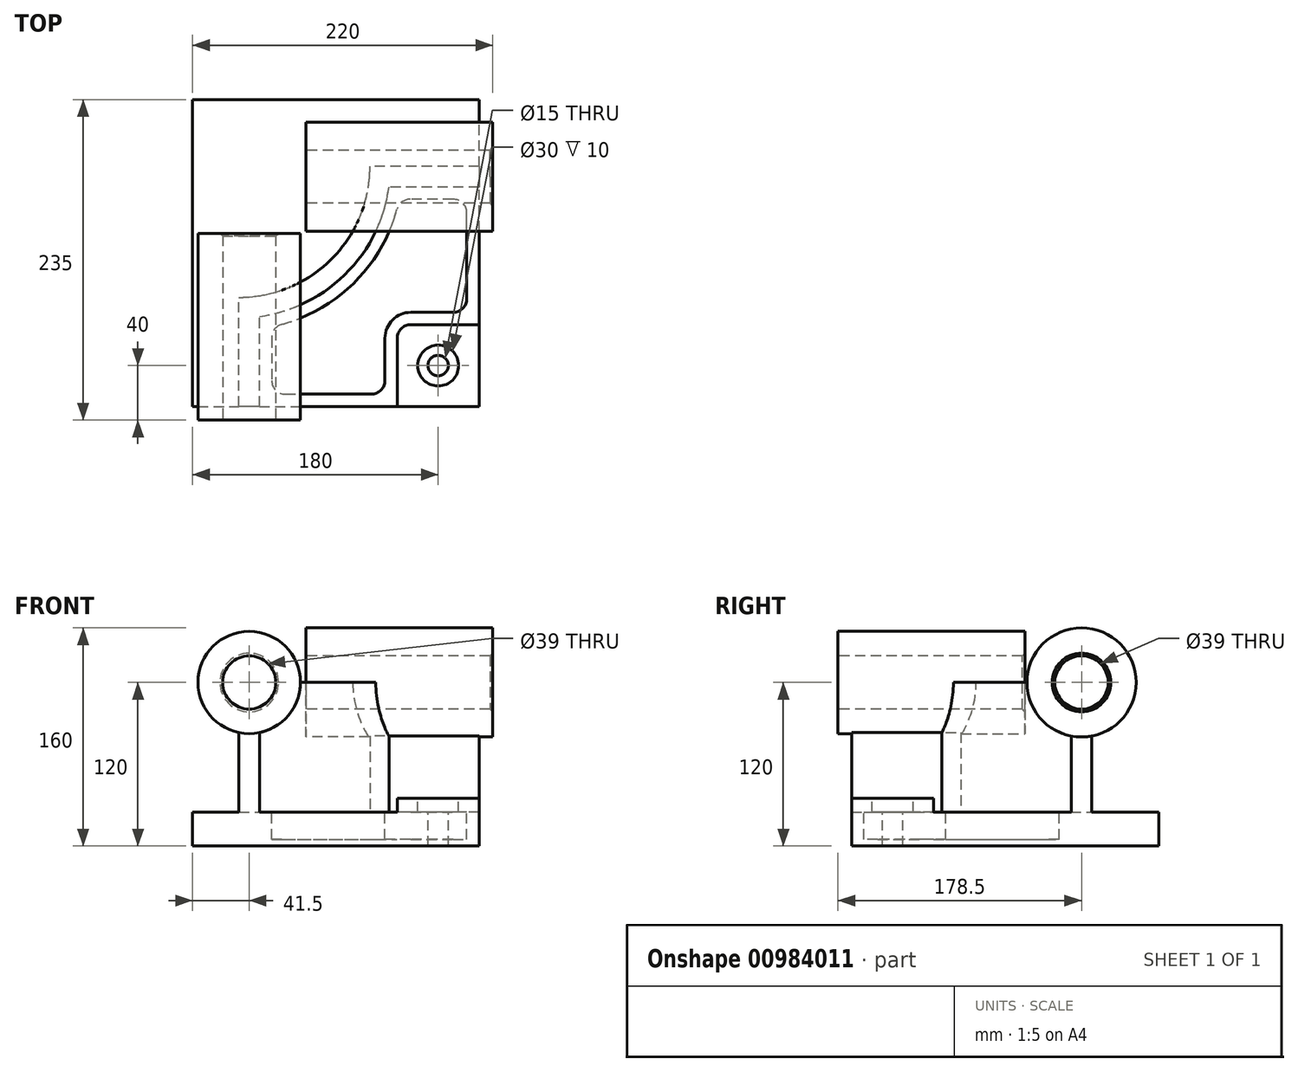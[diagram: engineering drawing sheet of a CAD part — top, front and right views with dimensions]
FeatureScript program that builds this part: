
annotation { "Feature Type Name" : "Feature", "Feature Type Description" : "" }
export const myFeature = defineFeature(function(context is Context, id is Id, definition is map)
    precondition{}
    {
        {
            var Q0;
            Q0=qCreatedBy(makeId("Top.planeOp"),FACE);
            var sketch = newSketch(context, id + "F0", { "sketchPlane" : qUnion([Q0])});
            skLineSegment(sketch, "E0.bottom", {"start": v(-105, -112.5) * mm, "end": v(105, -112.5) * mm});
            skLineSegment(sketch, "E0.top", {"start": v(-105, 112.5) * mm, "end": v(105, 112.5) * mm});
            skLineSegment(sketch, "E0.left", {"start": v(-105, -112.5) * mm, "end": v(-105, 112.5) * mm});
            skLineSegment(sketch, "E0.right", {"start": v(105, -112.5) * mm, "end": v(105, 112.5) * mm});
            skPoint(sketch, "E0.middle", {"position": v(0, 0) * mm});
            skSolve(sketch);
        }
        {
            var Q0;
            Q0=makeQuery(id+"F0.imprint","IMPRINT",FACE,{"disambiguationData":[TD([[makeQuery(id+"F0.imprint","IMPRINT",EDGE,{"derivedFrom":sQuery(id+"F0.wireOp",EDGE,"E0.bottom")}),1.0]])]});
            extrude(context, id + "F1", {"entities" : qUnion([Q0]), "depth" : 25 * mm, "offsetDistance" : 25 * mm});
        }
        {
            var Q0;
            Q0=makeQuery(id+"F1.opExtrude","CAP_FACE",FACE,{"disambiguationData":[OSD([sQuery(id+"F0.wireOp",EDGE,"E0.bottom"),sQuery(id+"F0.wireOp",EDGE,"E0.top"),sQuery(id+"F0.wireOp",EDGE,"E0.left"),sQuery(id+"F0.wireOp",EDGE,"E0.right")])],"isStart":false});
            var sketch = newSketch(context, id + "F2", { "sketchPlane" : qUnion([Q0])});
            skLineSegment(sketch, "E1", {"start": v(-71, -112.5) * mm, "end": v(-71, -32.5) * mm});
            skLineSegment(sketch, "E2", {"start": v(105, 63.5) * mm, "end": v(25, 63.5) * mm});
            skArc(sketch, "E3", {"start": v(-71, -32.5) * mm, "mid": v(-3.12, -4.38) * mm, "end": v(25, 63.5) * mm});
            skLineSegment(sketch, "E4", {"start": v(-71, 63.5) * mm, "end": v(25, 63.5) * mm, "construction": true});
            skLineSegment(sketch, "E5", {"start": v(-71, 63.5) * mm, "end": v(-71, -32.5) * mm, "construction": true});
            skLineSegment(sketch, "E6.0", {"start": v(-56, -112.5) * mm, "end": v(-56, -46.48) * mm});
            skArc(sketch, "E6.1", {"start": v(-56, -46.48) * mm, "mid": v(7.49, -14.99) * mm, "end": v(38.98, 48.5) * mm});
            skLineSegment(sketch, "E6.2", {"start": v(105, 48.5) * mm, "end": v(38.98, 48.5) * mm});
            skSolve(sketch);
        }
        {
            var Q0;
            {var subQ4=sQuery(id+"F2.wireOp",EDGE,"E1");Q0=makeQuery(id+"F2.imprint","IMPRINT",FACE,{"disambiguationData":[TD([[makeQuery(id+"F2.imprint","IMPRINT",EDGE,{"derivedFrom":subQ4}),-1.0]])]});}
            extrude(context, id + "F3", {"entities" : qUnion([Q0]), "operationType" : NewBodyOperationType.ADD, "depth" : 95 * mm, "offsetDistance" : 25 * mm});
        }
        {
            var Q0;
            {var subQ0=sQuery(id+"F0.wireOp",EDGE,"E0.bottom");Q0=makeQuery(id+"F3.boolean.opBoolean","MERGE",FACE,{"derivedFrom":[makeQuery(id+"F1.opExtrude","SWEPT_FACE",FACE,{"disambiguationData":[OSD([subQ0])]}),makeQuery(id+"F3.opExtrude","SWEPT_FACE",FACE,{"disambiguationData":[OSD([subQ0])]})]});}
            var sketch = newSketch(context, id + "F4", { "sketchPlane" : qUnion([Q0])});
            skCircle(sketch, "E7", {"center": v(-63.5, 120) * mm, "radius": 37.5 * mm});
            skSolve(sketch);
        }
        {
            var Q0;
            {var subQ1=sQuery(id+"F0.wireOp",EDGE,"E0.bottom");var subQ6=makeQuery(id+"F3.opExtrude","CAP_EDGE",EDGE,{"disambiguationData":[OSD([subQ1])],"isStart":false});Q0=makeQuery(id+"F4.imprint","IMPRINT",FACE,{"disambiguationData":[TD([[makeQuery(id+"F4.imprint","IMPRINT",EDGE,{"derivedFrom":subQ6}),1.0]])]});}
            var Q1;
            {var subQ1=sQuery(id+"F0.wireOp",EDGE,"E0.bottom");var subQ6=makeQuery(id+"F3.opExtrude","CAP_EDGE",EDGE,{"disambiguationData":[OSD([subQ1])],"isStart":false});Q1=makeQuery(id+"F4.imprint","IMPRINT",FACE,{"disambiguationData":[TD([[makeQuery(id+"F4.imprint","IMPRINT",EDGE,{"derivedFrom":subQ6}),-1.0]])]});}
            extrude(context, id + "F5", {"entities" : qUnion([Q0, Q1]), "operationType" : NewBodyOperationType.ADD, "depth" : 10 * mm, "offsetDistance" : 25 * mm, "hasSecondDirection" : true, "secondDirectionOppositeDirection" : true, "secondDirectionDepth" : 127 * mm});
        }
        {
            var Q0;
            {var subQ0=sQuery(id+"F0.wireOp",EDGE,"E0.right");Q0=makeQuery(id+"F3.boolean.opBoolean","MERGE",FACE,{"derivedFrom":[makeQuery(id+"F1.opExtrude","SWEPT_FACE",FACE,{"disambiguationData":[OSD([subQ0])]}),makeQuery(id+"F3.opExtrude","SWEPT_FACE",FACE,{"disambiguationData":[OSD([subQ0])]})]});}
            var sketch = newSketch(context, id + "F6", { "sketchPlane" : qUnion([Q0])});
            skCircle(sketch, "E8", {"center": v(56, 120) * mm, "radius": 40 * mm});
            skSolve(sketch);
        }
        {
            var Q0;
            {var subQ1=sQuery(id+"F0.wireOp",EDGE,"E0.right");var subQ6=makeQuery(id+"F3.opExtrude","CAP_EDGE",EDGE,{"disambiguationData":[OSD([subQ1])],"isStart":false});Q0=makeQuery(id+"F6.imprint","IMPRINT",FACE,{"disambiguationData":[TD([[makeQuery(id+"F6.imprint","IMPRINT",EDGE,{"derivedFrom":subQ6}),1.0]])]});}
            var Q1;
            {var subQ1=sQuery(id+"F0.wireOp",EDGE,"E0.right");var subQ6=makeQuery(id+"F3.opExtrude","CAP_EDGE",EDGE,{"disambiguationData":[OSD([subQ1])],"isStart":false});Q1=makeQuery(id+"F6.imprint","IMPRINT",FACE,{"disambiguationData":[TD([[makeQuery(id+"F6.imprint","IMPRINT",EDGE,{"derivedFrom":subQ6}),-1.0]])]});}
            extrude(context, id + "F7", {"entities" : qUnion([Q0, Q1]), "operationType" : NewBodyOperationType.ADD, "depth" : 10 * mm, "offsetDistance" : 25 * mm, "hasSecondDirection" : true, "secondDirectionOppositeDirection" : true, "secondDirectionDepth" : 127 * mm});
        }
        {
            var Q0;
            {var subQ0=sQuery(id+"F0.wireOp",EDGE,"E0.right");var subQ1=sQuery(id+"F0.wireOp",EDGE,"E0.bottom");Q0=makeQuery(id+"F3.boolean.opBoolean","SPLIT",FACE,{"disambiguationData":[TD([makeQuery(id+"F3.opExtrude","SWEPT_FACE",FACE,{"disambiguationData":[OSD([sQuery(id+"F2.wireOp",EDGE,"E6.0")])]})])],"derivedFrom":makeQuery(id+"F1.opExtrude","CAP_FACE",FACE,{"disambiguationData":[OSD([subQ1,sQuery(id+"F0.wireOp",EDGE,"E0.top"),sQuery(id+"F0.wireOp",EDGE,"E0.left"),subQ0])],"isStart":false})});}
            var sketch = newSketch(context, id + "F8", { "sketchPlane" : qUnion([Q0])});
            skLineSegment(sketch, "E9.bottom", {"start": v(105, -112.5) * mm, "end": v(45, -112.5) * mm});
            skLineSegment(sketch, "E9.top", {"start": v(105, -52.5) * mm, "end": v(45, -52.5) * mm});
            skLineSegment(sketch, "E9.left", {"start": v(105, -112.5) * mm, "end": v(105, -52.5) * mm});
            skLineSegment(sketch, "E9.right", {"start": v(45, -112.5) * mm, "end": v(45, -52.5) * mm});
            skSolve(sketch);
        }
        {
            var Q0;
            Q0=makeQuery(id+"F8.imprint","IMPRINT",FACE,{"disambiguationData":[TD([[makeQuery(id+"F8.imprint","IMPRINT",EDGE,{"derivedFrom":sQuery(id+"F8.wireOp",EDGE,"E9.bottom")}),1.0]])]});
            extrude(context, id + "F9", {"entities" : qUnion([Q0]), "operationType" : NewBodyOperationType.ADD, "depth" : 10 * mm, "offsetDistance" : 25 * mm});
        }
        {
            var Q0;
            Q0=makeQuery(id+"F9.opExtrude","SWEPT_EDGE",EDGE,{"disambiguationData":[OSD([sQuery(id+"F8.wireOp",EDGE,"E9.top"),sQuery(id+"F8.wireOp",EDGE,"E9.right")])]});
            fillet(context, id + "F10", {"entities" : qUnion([Q0]), "radius" : 10 * mm, "tangentPropagation" : true, "allowEdgeOverflow" : false});
        }
        {
            var Q0;
            {var subQ0=sQuery(id+"F0.wireOp",EDGE,"E0.right");var subQ1=sQuery(id+"F0.wireOp",EDGE,"E0.bottom");Q0=makeQuery(id+"F3.boolean.opBoolean","SPLIT",FACE,{"disambiguationData":[TD([makeQuery(id+"F3.opExtrude","SWEPT_FACE",FACE,{"disambiguationData":[OSD([sQuery(id+"F2.wireOp",EDGE,"E6.0")])]})])],"derivedFrom":makeQuery(id+"F1.opExtrude","CAP_FACE",FACE,{"disambiguationData":[OSD([subQ1,sQuery(id+"F0.wireOp",EDGE,"E0.top"),sQuery(id+"F0.wireOp",EDGE,"E0.left"),subQ0])],"isStart":false})});}
            var sketch = newSketch(context, id + "F11", { "sketchPlane" : qUnion([Q0])});
            skLineSegment(sketch, "E10.0", {"start": v(-47, -54.08) * mm, "end": v(-47, -103.5) * mm});
            skArc(sketch, "E10.1", {"start": v(46.58, 39.5) * mm, "mid": v(13.85, -21.35) * mm, "end": v(-47, -54.08) * mm});
            skLineSegment(sketch, "E10.2", {"start": v(-47, -103.5) * mm, "end": v(36, -103.5) * mm});
            skLineSegment(sketch, "E10.3", {"start": v(96, 39.5) * mm, "end": v(46.58, 39.5) * mm});
            skLineSegment(sketch, "E10.4", {"start": v(36, -103.5) * mm, "end": v(36, -62.5) * mm});
            skArc(sketch, "E10.5", {"start": v(36, -62.5) * mm, "mid": v(41.56, -49.06) * mm, "end": v(55, -43.5) * mm});
            skLineSegment(sketch, "E10.6", {"start": v(55, -43.5) * mm, "end": v(96, -43.5) * mm});
            skLineSegment(sketch, "E10.7", {"start": v(96, -43.5) * mm, "end": v(96, 39.5) * mm});
            skLineSegment(sketch, "E11.0", {"start": v(-61, -42.03) * mm, "end": v(-61, -117.5) * mm});
            skArc(sketch, "E11.1", {"start": v(34.53, 53.5) * mm, "mid": v(3.95, -11.45) * mm, "end": v(-61, -42.03) * mm});
            skLineSegment(sketch, "E11.2", {"start": v(-61, -117.5) * mm, "end": v(50, -117.5) * mm});
            skLineSegment(sketch, "E11.3", {"start": v(110, 53.5) * mm, "end": v(34.53, 53.5) * mm});
            skLineSegment(sketch, "E11.4", {"start": v(50, -117.5) * mm, "end": v(50, -62.5) * mm});
            skArc(sketch, "E11.5", {"start": v(50, -62.5) * mm, "mid": v(51.46, -58.96) * mm, "end": v(55, -57.5) * mm});
            skLineSegment(sketch, "E11.6", {"start": v(55, -57.5) * mm, "end": v(110, -57.5) * mm});
            skLineSegment(sketch, "E11.7", {"start": v(110, -57.5) * mm, "end": v(110, 53.5) * mm});
            skSolve(sketch);
        }
        {
            var Q0;
            Q0=makeQuery(id+"F11.imprint","IMPRINT",FACE,{"disambiguationData":[TD([[makeQuery(id+"F11.imprint","IMPRINT",EDGE,{"derivedFrom":sQuery(id+"F11.wireOp",EDGE,"E10.0")}),1.0]])]});
            extrude(context, id + "F12", {"entities" : qUnion([Q0]), "operationType" : NewBodyOperationType.REMOVE, "oppositeDirection" : true, "depth" : 20 * mm, "offsetDistance" : 25 * mm});
        }
        {
            var Q0;
            Q0=makeQuery(id+"F9.opExtrude","CAP_FACE",FACE,{"disambiguationData":[OSD([sQuery(id+"F8.wireOp",EDGE,"E9.bottom"),sQuery(id+"F8.wireOp",EDGE,"E9.top"),sQuery(id+"F8.wireOp",EDGE,"E9.left"),sQuery(id+"F8.wireOp",EDGE,"E9.right")])],"isStart":false});
            var sketch = newSketch(context, id + "F13", { "sketchPlane" : qUnion([Q0])});
            skCircle(sketch, "E12", {"center": v(75, -82.5) * mm, "radius": 15 * mm});
            skSolve(sketch);
        }
        {
            var Q0;
            Q0=sQuery(id+"F13.wireOp",VERTEX,"E12.center");
            var Q1;
            Q1=makeQuery(id+"F1.opExtrude","SWEPT_BODY",BODY,{"disambiguationData":[OSD([sQuery(id+"F0.wireOp",EDGE,"E0.bottom"),sQuery(id+"F0.wireOp",EDGE,"E0.top"),sQuery(id+"F0.wireOp",EDGE,"E0.left"),sQuery(id+"F0.wireOp",EDGE,"E0.right")])]});
            hole(context, id + "F14", {"style" : HoleStyle.C_BORE, "endStyle" : HoleEndStyle.THROUGH, "holeDiameter" : 15 * mm, "cBoreDiameter" : 30 * mm, "cBoreDepth" : 10 * mm, "majorDiameter" : 5 * mm, "isTappedThrough" : true, "tappedDepth" : 12 * mm, "tapClearance" : 3, "locations" : qUnion([Q0]), "scope" : qUnion([Q1])});
        }
        {
            var Q0;
            Q0=makeQuery(id+"F12.boolean.opBoolean","COPY",EDGE,{"derivedFrom":makeQuery(id+"F12.opExtrude","SWEPT_EDGE",EDGE,{"disambiguationData":[OSD([sQuery(id+"F11.wireOp",EDGE,"E10.0"),sQuery(id+"F11.wireOp",EDGE,"E10.1")])]})});
            var Q1;
            Q1=makeQuery(id+"F12.boolean.opBoolean","COPY",EDGE,{"derivedFrom":makeQuery(id+"F12.opExtrude","SWEPT_EDGE",EDGE,{"disambiguationData":[OSD([sQuery(id+"F11.wireOp",EDGE,"E10.0"),sQuery(id+"F11.wireOp",EDGE,"E10.2")])]})});
            var Q2;
            Q2=makeQuery(id+"F12.boolean.opBoolean","COPY",EDGE,{"derivedFrom":makeQuery(id+"F12.opExtrude","SWEPT_EDGE",EDGE,{"disambiguationData":[OSD([sQuery(id+"F11.wireOp",EDGE,"E10.2"),sQuery(id+"F11.wireOp",EDGE,"E10.4")])]})});
            var Q3;
            Q3=makeQuery(id+"F12.boolean.opBoolean","COPY",EDGE,{"derivedFrom":makeQuery(id+"F12.opExtrude","SWEPT_EDGE",EDGE,{"disambiguationData":[OSD([sQuery(id+"F11.wireOp",EDGE,"E10.1"),sQuery(id+"F11.wireOp",EDGE,"E10.3")])]})});
            var Q4;
            Q4=makeQuery(id+"F12.boolean.opBoolean","COPY",EDGE,{"derivedFrom":makeQuery(id+"F12.opExtrude","SWEPT_EDGE",EDGE,{"disambiguationData":[OSD([sQuery(id+"F11.wireOp",EDGE,"E10.3"),sQuery(id+"F11.wireOp",EDGE,"E10.7")])]})});
            var Q5;
            Q5=makeQuery(id+"F12.boolean.opBoolean","COPY",EDGE,{"derivedFrom":makeQuery(id+"F12.opExtrude","SWEPT_EDGE",EDGE,{"disambiguationData":[OSD([sQuery(id+"F11.wireOp",EDGE,"E10.6"),sQuery(id+"F11.wireOp",EDGE,"E10.7")])]})});
            fillet(context, id + "F15", {"entities" : qUnion([Q0, Q1, Q2, Q3, Q4, Q5]), "radius" : 10 * mm, "tangentPropagation" : true, "allowEdgeOverflow" : false});
        }
        {
            var Q0;
            Q0=makeQuery(id+"F5.opExtrude","CAP_FACE",FACE,{"disambiguationData":[OSD([sQuery(id+"F4.wireOp",EDGE,"E7")])],"isStart":false});
            var sketch = newSketch(context, id + "F16", { "sketchPlane" : qUnion([Q0])});
            skCircle(sketch, "E13", {"center": v(-63.5, 120) * mm, "radius": 19.5 * mm});
            skSolve(sketch);
        }
        {
            var Q0;
            Q0=makeQuery(id+"F16.imprint","IMPRINT",FACE,{"disambiguationData":[TD([[makeQuery(id+"F16.imprint","IMPRINT",EDGE,{"derivedFrom":sQuery(id+"F16.wireOp",EDGE,"E13")}),1.0]])]});
            extrude(context, id + "F17", {"entities" : qUnion([Q0]), "operationType" : NewBodyOperationType.REMOVE, "endBound" : BoundingType.THROUGH_ALL, "oppositeDirection" : true, "depth" : 25 * mm, "offsetDistance" : 25 * mm});
        }
        {
            var Q0;
            Q0=makeQuery(id+"F7.opExtrude","CAP_FACE",FACE,{"disambiguationData":[OSD([sQuery(id+"F6.wireOp",EDGE,"E8")])],"isStart":true});
            var sketch = newSketch(context, id + "F18", { "sketchPlane" : qUnion([Q0])});
            skCircle(sketch, "E14", {"center": v(-56, 120) * mm, "radius": 19.5 * mm});
            skSolve(sketch);
        }
        {
            var Q0;
            Q0=makeQuery(id+"F18.imprint","IMPRINT",FACE,{"disambiguationData":[TD([[makeQuery(id+"F18.imprint","IMPRINT",EDGE,{"derivedFrom":sQuery(id+"F18.wireOp",EDGE,"E14")}),1.0]])]});
            extrude(context, id + "F19", {"entities" : qUnion([Q0]), "operationType" : NewBodyOperationType.REMOVE, "endBound" : BoundingType.THROUGH_ALL, "oppositeDirection" : true, "depth" : 25 * mm, "offsetDistance" : 25 * mm});
        }
        {
            var Q0;
            Q0=makeQuery(id+"F19.boolean.opBoolean","COPY",EDGE,{"derivedFrom":makeQuery(id+"F19.opExtrude","CAP_EDGE",EDGE,{"disambiguationData":[OSD([sQuery(id+"F18.wireOp",EDGE,"E14")])],"isStart":true})});
            var Q1;
            Q1=makeQuery(id+"F17.boolean.opBoolean","INTERSECT",EDGE,{"derivedFrom":[makeQuery(id+"F5.opExtrude","CAP_FACE",FACE,{"disambiguationData":[OSD([sQuery(id+"F4.wireOp",EDGE,"E7")])],"isStart":true}),makeQuery(id+"F17.opExtrude","SWEPT_FACE",FACE,{"disambiguationData":[OSD([sQuery(id+"F16.wireOp",EDGE,"E13")])]})]});
            var Q2;
            Q2=makeQuery(id+"F17.boolean.opBoolean","COPY",EDGE,{"derivedFrom":makeQuery(id+"F17.opExtrude","CAP_EDGE",EDGE,{"disambiguationData":[OSD([sQuery(id+"F16.wireOp",EDGE,"E13")])],"isStart":true})});
            var Q3;
            Q3=makeQuery(id+"F19.boolean.opBoolean","INTERSECT",EDGE,{"derivedFrom":[makeQuery(id+"F7.opExtrude","CAP_FACE",FACE,{"disambiguationData":[OSD([sQuery(id+"F6.wireOp",EDGE,"E8")])],"isStart":false}),makeQuery(id+"F19.opExtrude","SWEPT_FACE",FACE,{"disambiguationData":[OSD([sQuery(id+"F18.wireOp",EDGE,"E14")])]})]});
            chamfer(context, id + "F20", {"entities" : qUnion([Q0, Q1, Q2, Q3]), "width" : 2 * mm, "tangentPropagation" : true});
        }
    });
